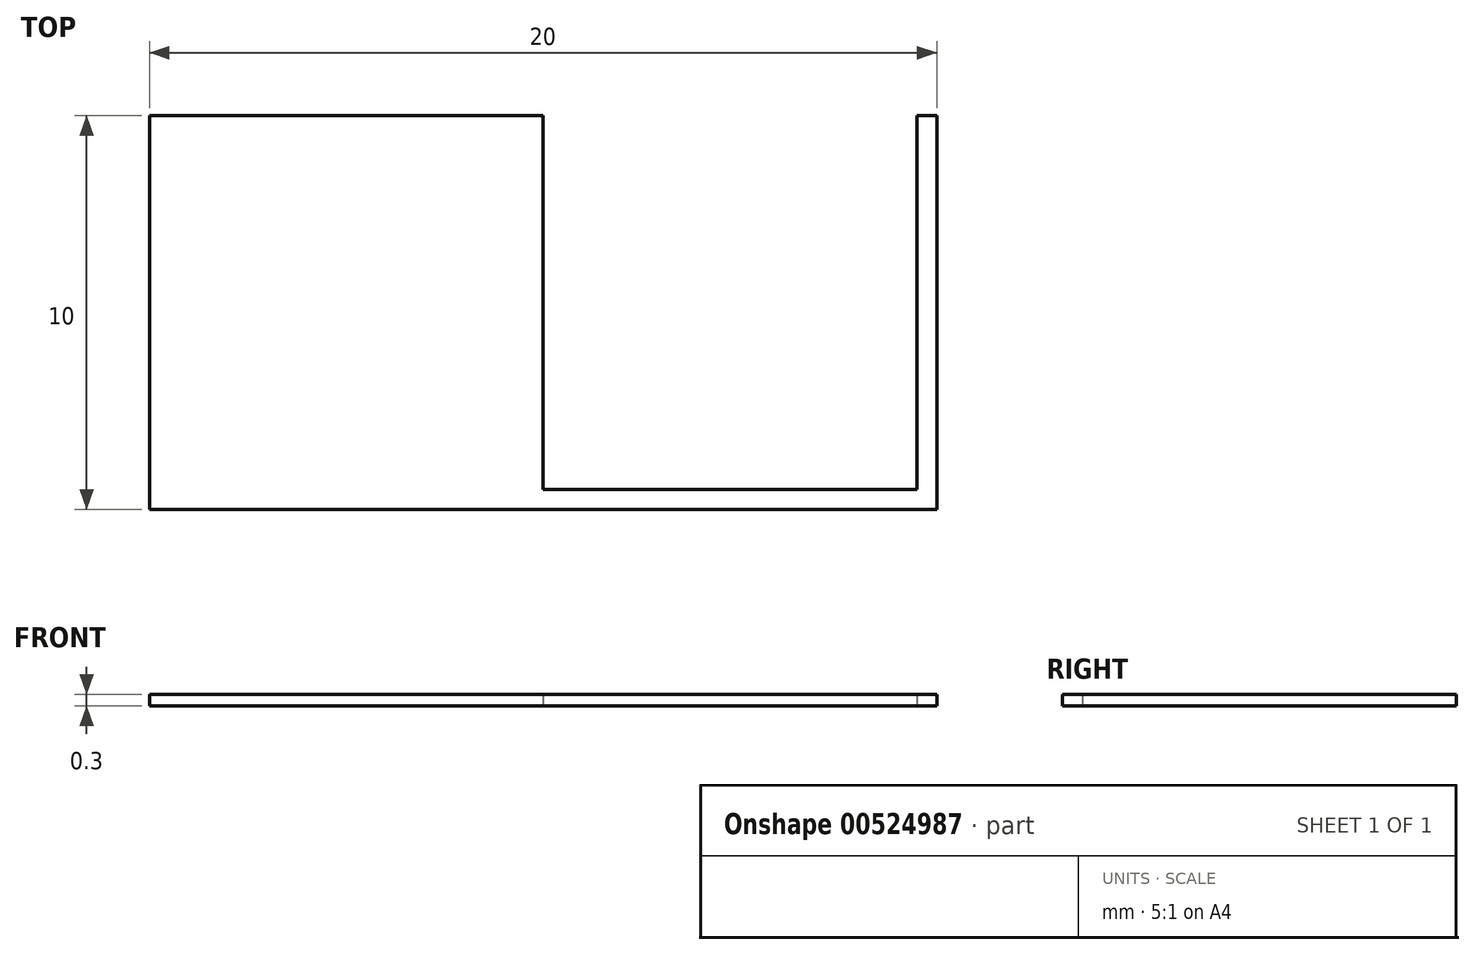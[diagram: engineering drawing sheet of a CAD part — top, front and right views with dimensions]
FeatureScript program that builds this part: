
annotation { "Feature Type Name" : "Feature", "Feature Type Description" : "" }
export const myFeature = defineFeature(function(context is Context, id is Id, definition is map)
    precondition{}
    {
        {
            var Q0;
            Q0=qCreatedBy(makeId("Top.planeOp"),FACE);
            var sketch = newSketch(context, id + "F0", { "sketchPlane" : qUnion([Q0])});
            skLineSegment(sketch, "E0.bottom", {"start": v(-5, 5) * mm, "end": v(5, 5) * mm});
            skLineSegment(sketch, "E0.top", {"start": v(-5, -5) * mm, "end": v(5, -5) * mm});
            skLineSegment(sketch, "E0.left", {"start": v(-5, 5) * mm, "end": v(-5, -5) * mm});
            skLineSegment(sketch, "E0.right", {"start": v(5, 5) * mm, "end": v(5, -5) * mm});
            skPoint(sketch, "E1", {"position": v(0, 5) * mm});
            skPoint(sketch, "E2", {"position": v(-5, 0) * mm});
            skLineSegment(sketch, "E3.bottom", {"start": v(5, -4.5) * mm, "end": v(15, -4.5) * mm});
            skLineSegment(sketch, "E3.top", {"start": v(5, -5) * mm, "end": v(15, -5) * mm});
            skLineSegment(sketch, "E3.left", {"start": v(5, -4.5) * mm, "end": v(5, -5) * mm});
            skLineSegment(sketch, "E3.right", {"start": v(15, -4.5) * mm, "end": v(15, -5) * mm});
            skLineSegment(sketch, "E4.bottom", {"start": v(15, -4.5) * mm, "end": v(14.5, -4.5) * mm});
            skLineSegment(sketch, "E4.top", {"start": v(15, 5) * mm, "end": v(14.5, 5) * mm});
            skLineSegment(sketch, "E4.left", {"start": v(15, -4.5) * mm, "end": v(15, 5) * mm});
            skLineSegment(sketch, "E4.right", {"start": v(14.5, -4.5) * mm, "end": v(14.5, 5) * mm});
            skSolve(sketch);
        }
        {
            var Q0;
            Q0 = qSketchRegion(id + "F0", true);
            extrude(context, id + "F1", {"entities" : qUnion([Q0]), "depth" : 0.3 * mm, "offsetDistance" : 25 * mm});
        }
    });
